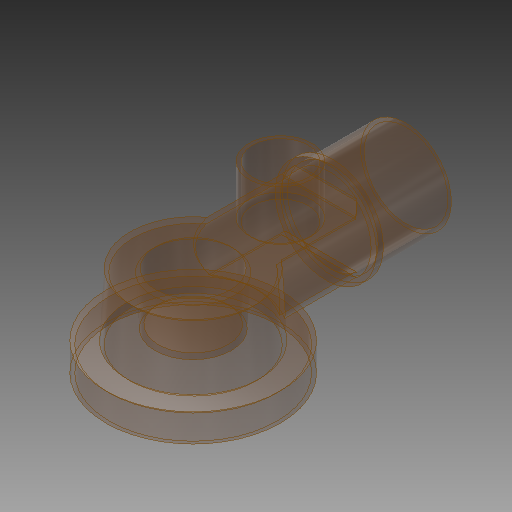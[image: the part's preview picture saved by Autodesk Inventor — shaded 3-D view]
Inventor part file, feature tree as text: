
AUTODESK INVENTOR PART (.ipt)
format: ipt  version: 2019 (Build 230136000, 136)  size: 250,880 bytes
history: native  units: mm
features: extrude x9, sketch x9, other x5, chamfer x1, shell x1
ambient origin geometry x8: Origin, YZ Plane, XZ Plane, XY Plane, X Axis, Y Axis, Z Axis, Center Point
bodies: Body1 (feature_tree)
feature tree (25):
  other  "Sólido1"
  extrude  "Extrusão1"  Depth=1.0mm
  extrude  "Extrusão2"  Depth=23.0mm
  extrude  "Extrusão3"  Depth=38.0mm TaperAngle=0.0deg
  other  "Face para inclinação de faces1"
  extrude  "Extrusão4"  Depth=18.0mm TaperAngle=0.0deg
  chamfer  "Chanfro1"  Distance=2.0mm
  extrude  "Extrusão5"  Depth=50.0mm
  extrude  "Extrusão6"  Depth=14.0mm
  other  "Face para inclinação de faces2"
  shell  "Casca1"  Thickness=14.0mm
  extrude  "Extrusão7"  Depth=1.0mm
  extrude  "Extrusão8"  Depth=1.0mm TaperAngle=0.0deg
  extrude  "Extrusão9"  Depth=18.0mm
  sketch  "Esboço1"  dims[d0=26.0mm d1=1.0mm]
  sketch  "Esboço2"  dims[d2=23.0mm d3=0.0mm d4=7.5mm]
  sketch  "Esboço3"  dims[d5=7.5mm d6=38.0mm d7=0.0mm]
  sketch  "Esboço4"  dims[d8=38.0mm d9=18.0mm d10=0.0mm]
  other  "Contorno projetado1"
  sketch  "Esboço5"  dims[d11=0.523599mm]
  sketch  "Esboço6"  dims[d12=1.5mm d13=2.0mm d14=0.0mm]
  sketch  "Esboço7"  dims[d15=2.0mm d16=2.0mm d17=45.0deg d18=50.0mm]
  sketch  "Esboço8"  dims[d19=8.0mm d20=0.0mm d21=20.0mm d22=14.0mm d23=0.0mm]
  sketch  "Esboço9"  dims[d24=0.523599mm d27=1.0mm d28=2.0mm d29=0.0mm d30=18.0mm d31=14.0mm d32=0.0mm d33=1.0mm d34=16.0mm d35=0.0mm]
  other  "Contorno projetado2"
